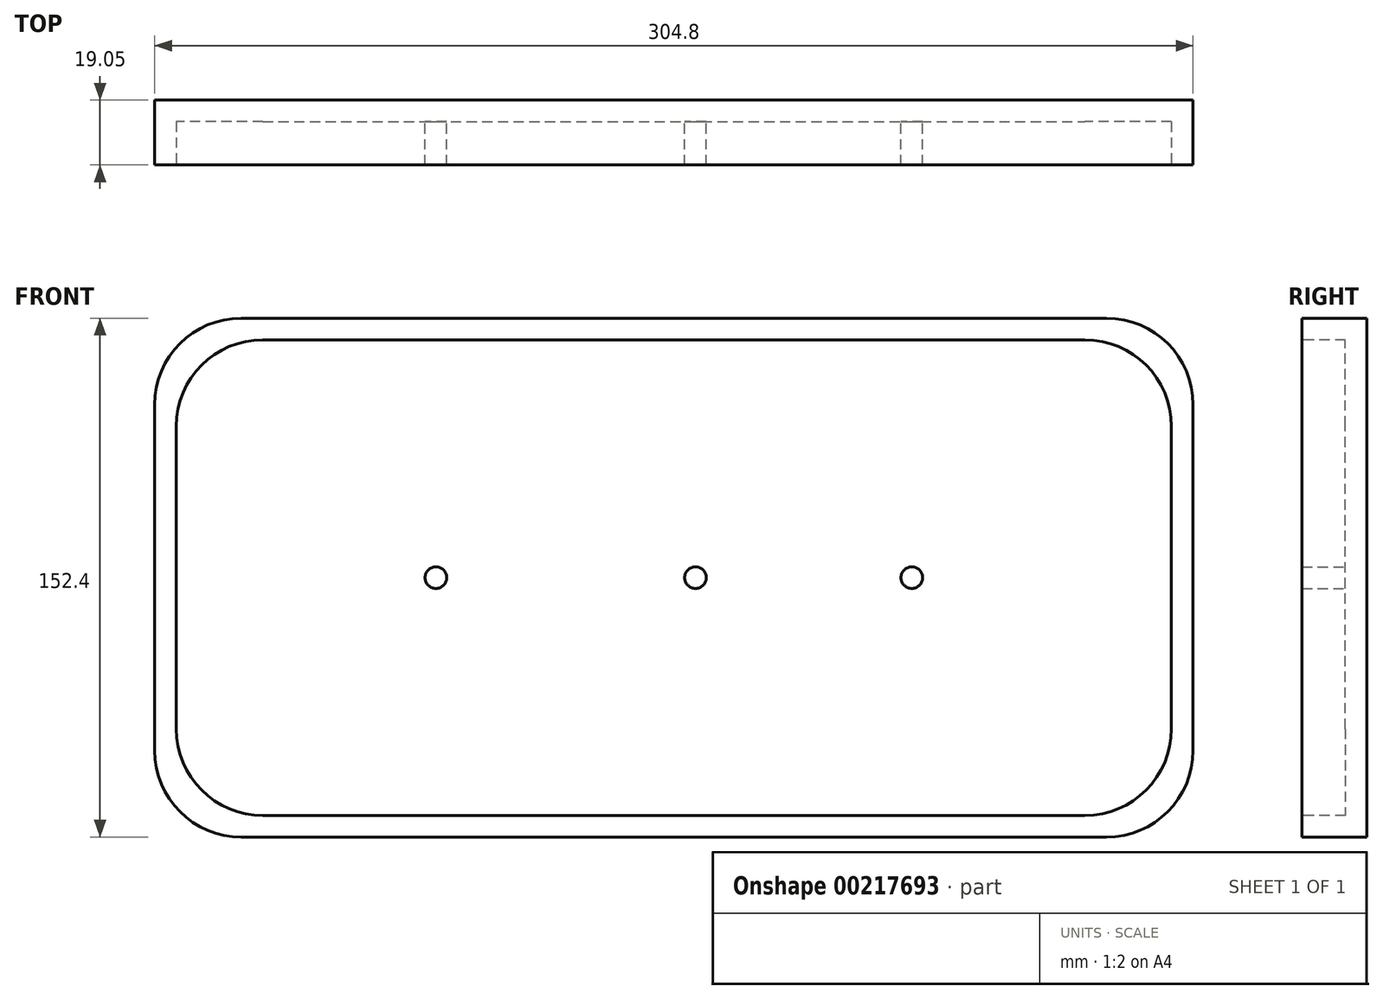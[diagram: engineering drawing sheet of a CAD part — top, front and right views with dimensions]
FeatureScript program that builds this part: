
annotation { "Feature Type Name" : "Feature", "Feature Type Description" : "" }
export const myFeature = defineFeature(function(context is Context, id is Id, definition is map)
    precondition{}
    {
        {
            var Q0;
            Q0=qCreatedBy(makeId("Front.planeOp"),FACE);
            var sketch = newSketch(context, id + "F0", { "sketchPlane" : qUnion([Q0])});
            skLineSegment(sketch, "E0.bottom", {"start": v(25.4, 0) * mm, "end": v(279.4, 0) * mm});
            skLineSegment(sketch, "E0.top", {"start": v(25.4, 152.4) * mm, "end": v(279.4, 152.4) * mm});
            skLineSegment(sketch, "E0.left", {"start": v(0, 25.4) * mm, "end": v(0, 127) * mm});
            skLineSegment(sketch, "E0.right", {"start": v(304.8, 25.4) * mm, "end": v(304.8, 127) * mm});
            skPoint(sketch, "E1.visualSharp", {"position": v(0, 152.4) * mm});
            skArc(sketch, "E1.filletArc", {"start": v(25.4, 152.4) * mm, "mid": v(7.44, 144.96) * mm, "end": v(0, 127) * mm});
            skPoint(sketch, "E2.visualSharp", {"position": v(304.8, 152.4) * mm});
            skArc(sketch, "E2.filletArc", {"start": v(304.8, 127) * mm, "mid": v(297.36, 144.96) * mm, "end": v(279.4, 152.4) * mm});
            skPoint(sketch, "E3.visualSharp", {"position": v(304.8, 0) * mm});
            skArc(sketch, "E3.filletArc", {"start": v(279.4, 0) * mm, "mid": v(297.36, 7.44) * mm, "end": v(304.8, 25.4) * mm});
            skPoint(sketch, "E4.visualSharp", {"position": v(0, 0) * mm});
            skArc(sketch, "E4.filletArc", {"start": v(0, 25.4) * mm, "mid": v(7.44, 7.44) * mm, "end": v(25.4, 0) * mm});
            skSolve(sketch);
        }
        {
            var Q0;
            Q0 = qSketchRegion(id + "F0", true);
            extrude(context, id + "F1", {"entities" : qUnion([Q0]), "depth" : 19.05 * mm});
        }
        {
            var Q0;
            Q0=makeQuery(id+"F1.opExtrude","CAP_FACE",FACE,{"disambiguationData":[OSD([sQuery(id+"F0.wireOp",EDGE,"E0.bottom"),sQuery(id+"F0.wireOp",EDGE,"E0.top"),sQuery(id+"F0.wireOp",EDGE,"E0.left"),sQuery(id+"F0.wireOp",EDGE,"E0.right"),sQuery(id+"F0.wireOp",EDGE,"E1.filletArc"),sQuery(id+"F0.wireOp",EDGE,"E2.filletArc"),sQuery(id+"F0.wireOp",EDGE,"E3.filletArc"),sQuery(id+"F0.wireOp",EDGE,"E4.filletArc")])],"isStart":false});
            var sketch = newSketch(context, id + "F2", { "sketchPlane" : qUnion([Q0])});
            skLineSegment(sketch, "E5.bottom", {"start": v(31.75, 6.35) * mm, "end": v(273.05, 6.35) * mm});
            skLineSegment(sketch, "E5.top", {"start": v(31.75, 146.05) * mm, "end": v(273.05, 146.05) * mm});
            skLineSegment(sketch, "E5.left", {"start": v(6.35, 31.75) * mm, "end": v(6.35, 120.65) * mm});
            skLineSegment(sketch, "E5.right", {"start": v(298.45, 31.75) * mm, "end": v(298.45, 120.65) * mm});
            skPoint(sketch, "E6.visualSharp", {"position": v(6.35, 146.05) * mm});
            skArc(sketch, "E6.filletArc", {"start": v(31.75, 146.05) * mm, "mid": v(13.79, 138.61) * mm, "end": v(6.35, 120.65) * mm});
            skPoint(sketch, "E7.visualSharp", {"position": v(298.45, 146.05) * mm});
            skArc(sketch, "E7.filletArc", {"start": v(298.45, 120.65) * mm, "mid": v(291.01, 138.61) * mm, "end": v(273.05, 146.05) * mm});
            skPoint(sketch, "E8.visualSharp", {"position": v(298.45, 6.35) * mm});
            skArc(sketch, "E8.filletArc", {"start": v(273.05, 6.35) * mm, "mid": v(291.01, 13.79) * mm, "end": v(298.45, 31.75) * mm});
            skPoint(sketch, "E9.visualSharp", {"position": v(6.35, 6.35) * mm});
            skArc(sketch, "E9.filletArc", {"start": v(6.35, 31.75) * mm, "mid": v(13.79, 13.79) * mm, "end": v(31.75, 6.35) * mm});
            skSolve(sketch);
        }
        {
            var Q0;
            Q0 = qSketchRegion(id + "F2", true);
            extrude(context, id + "F3", {"entities" : qUnion([Q0]), "operationType" : NewBodyOperationType.REMOVE, "oppositeDirection" : true, "depth" : 12.7 * mm});
        }
        {
            var Q0;
            Q0=makeQuery(id+"F3.boolean.opBoolean","COPY",FACE,{"derivedFrom":makeQuery(id+"F3.opExtrude","CAP_FACE",FACE,{"disambiguationData":[OSD([sQuery(id+"F2.wireOp",EDGE,"E5.bottom"),sQuery(id+"F2.wireOp",EDGE,"E5.top"),sQuery(id+"F2.wireOp",EDGE,"E5.left"),sQuery(id+"F2.wireOp",EDGE,"E5.right"),sQuery(id+"F2.wireOp",EDGE,"E6.filletArc"),sQuery(id+"F2.wireOp",EDGE,"E7.filletArc"),sQuery(id+"F2.wireOp",EDGE,"E8.filletArc"),sQuery(id+"F2.wireOp",EDGE,"E9.filletArc")])],"isStart":false})});
            var sketch = newSketch(context, id + "F4", { "sketchPlane" : qUnion([Q0])});
            skCircle(sketch, "E10", {"center": v(82.55, 76.2) * mm, "radius": 3.18 * mm});
            skCircle(sketch, "E11", {"center": v(158.75, 76.2) * mm, "radius": 3.18 * mm});
            skCircle(sketch, "E12", {"center": v(222.25, 76.2) * mm, "radius": 3.18 * mm});
            skSolve(sketch);
        }
        {
            var Q0;
            Q0 = qSketchRegion(id + "F4", true);
            extrude(context, id + "F5", {"entities" : qUnion([Q0]), "operationType" : NewBodyOperationType.ADD, "depth" : 12.7 * mm});
        }
    });
